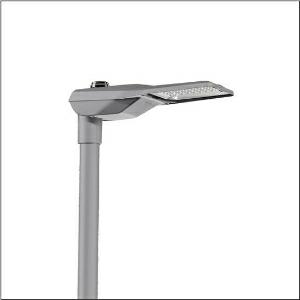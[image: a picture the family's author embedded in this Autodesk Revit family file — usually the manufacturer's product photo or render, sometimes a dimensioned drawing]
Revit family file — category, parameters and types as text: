
# Revit family: streetlight_sl_21_mini___st1_5a_5xe6p47n08hb_ac47
name_source: partatom
category: Lighting Fixtures
units: mm (PartAtom-declared; Revit-internal decimal feet)

## family parameters
Cut with Voids When Loaded = No
Host = Face
Light Source = No
Part Type = Normal
Room Calculation Point = No
Round Connector Dimension = Use Diameter
Shared = No

## types (1)
- --- (1 x LED, 9260 lm, 66 W, 4000K)
    Apparent Load = 66 VA
    CIE Flux Codes = 22 53 95 100 100
    Color Rendering = 70
    Color Temperature = 4000K
    Default Elevation = 1800 mm
    Description = Streetlight SL 21 mini, mast luminaire, primary light control with lens, of PMMA, primary optical cover: cover, of toughened safety glass, transparent, light distribution: ST1.5a, light emission: direct distribution, primary light characteristic: asymmetric, installation type: side-entry, LED, 3G 1.5mm², High Power LED, rated luminous flux: 9.260lm, luminous efficacy: 140lm/W, light colour: 740, colour temperature: 4000K, control gear: NEMA (7pin), control: overheat protection, pre-setting: linear dimming characteristic, constant luminous flux control, time-dependent luminous flux control, flexible luminous flux parameterisation, mains connection: 230..240V, AC, 50/60Hz, connection cable pre-assembled, cable length: 8,5m, wiring characteristics: H07RN-F, start of lifetime: 66W, end of service life: 69W, reduction: 30W, luminaire housing, of diecast aluminium (EN AC-44300), powder-coated, Siteco® metallic grey (DB 702S), corrosivity category C5 mid according to DIN EN ISO 12944, multi-level sealing system, sealing non-destructively replaceable, inclination adjustable: 0°, 5°, 10°, 15°, length: 628mm, width: 235mm, height: 110mm, spigot size: 42mm (side-entry), mounting height: 4..8m, protection rating (complete): IP66, insulation class (complete): insulation class I (protective earthing), certification: CE, ENEC, ENEC+, VDE, impact resistance: IK10, permissible operating ambient temperature for outdoor applications: -40..+50°C, standard-compliant lighting for roads and squares, packaging unit: 1 piece

Light Distribution: ST1.5a
    Height = 110 mm
    Lamp = 1 x LED
    Lamp Light Flux = 9260 lm
    Lamp Power = 66 W
    Lamp count = 1
    Length = 625 mm
    Luminous efficacy = 140 lm/W
    Manufacturer = Siteco
    ModVariant = No
    Model = 5XE6P47N08HB
    Number of Poles = 1
    OnlyDefault = Yes
    Power Factor = 1
    Product Name = Streetlight SL 21 mini | ST1.5a
    Product group = mast luminaire | pylon top
    ProductGroupID = 6100
    Protection Class = Protection class I
    Protection Degree = IP 66
    RLX_Detail_Level = 1
    RLX_Emergency_Light_Flux = 0 lm
    RLX_Emergency_Type = 0
    RLX_Emergency_Type_DB = No
    RlxData = <blob elided: 29661 chars, md5=2562a284>
    Socket = socket
    Standby Power = 0 W
    System Light Flux = 9260 lm
    System Power = 66 W
    Type Comments = factory setting: luminous flux: 100 % | dim-lin: 254 | 670 mA
    Type Image = l_1294379.jpg
    URL = http://relux.com
    VarID = @adj_133540
    Voltage = 0 V
    Weight = 0.00 kg
    Width = 234 mm

## geometry (parser evidence)
native form markers: Blend x4, Sweep x8
no freeform markers — native parametric forms only
